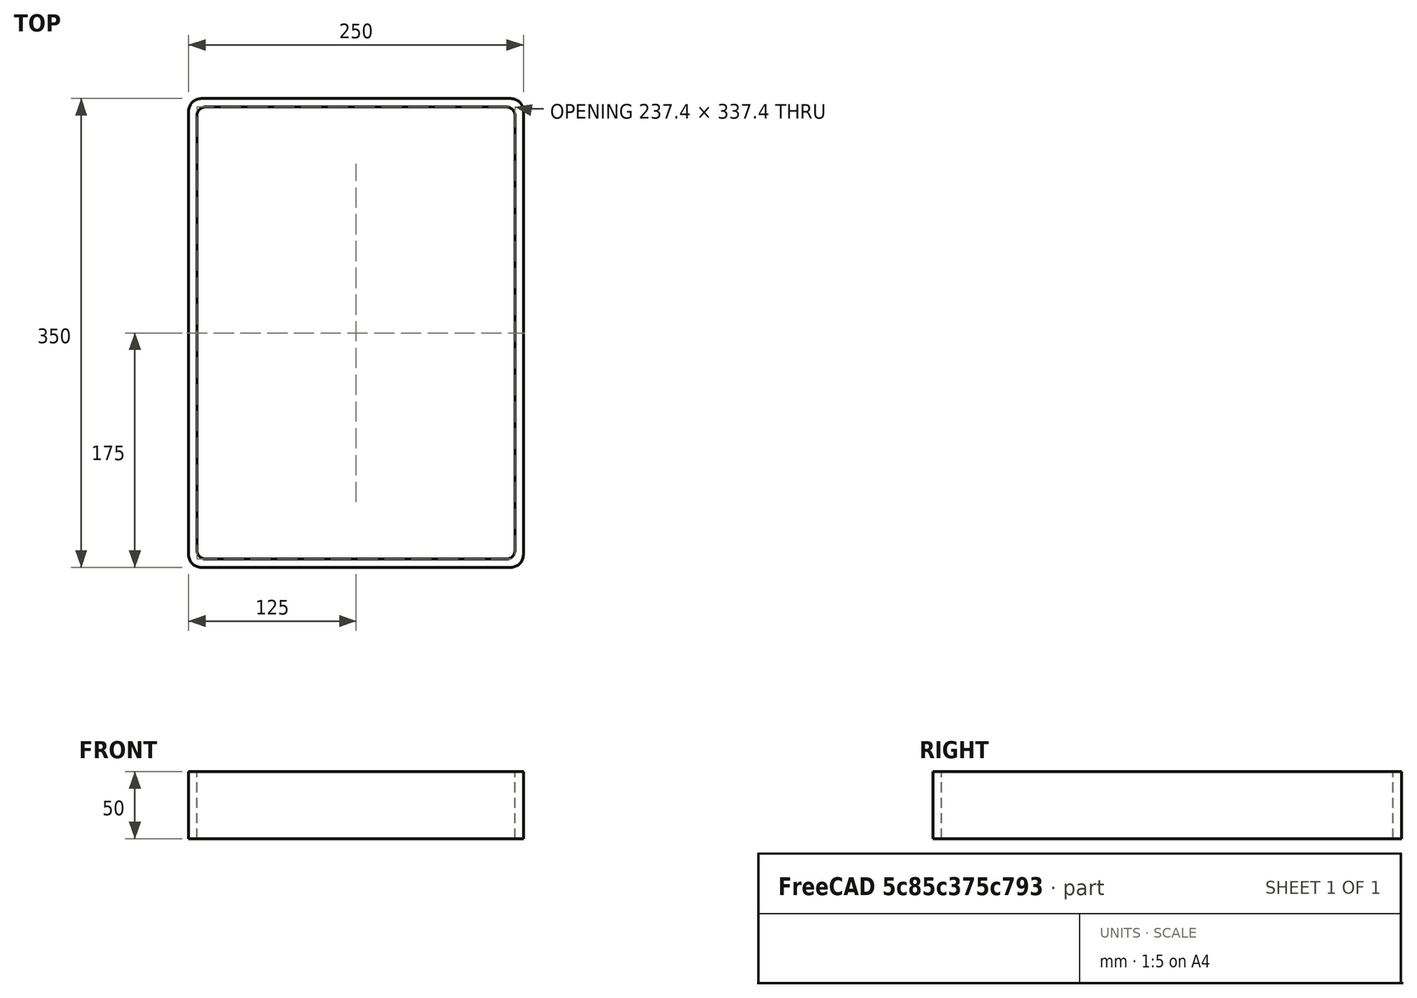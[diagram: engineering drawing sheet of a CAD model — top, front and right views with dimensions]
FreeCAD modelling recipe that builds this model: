
FCSTD DOCUMENT  (FreeCAD 0.15R4671 (Git))
Label: Rectangular hollow section 350x250x6.3 EN10219 S235JRH
License: All rights reserved
LicenseURL: http://en.wikipedia.org/wiki/All_rights_reserved
objects: Sketcher::SketchObject×1, Part::Extrusion×1
note: 2 computed .brp shape members not serialized (recipe doc carries the construction recipe); baked Part::Feature solids carry a one-line shape summary decoded from their .brp

FEATURE [Sketcher::SketchObject] Sketch
  sketch-geometry (16):
    g0: LineSegment StartX=-112.4 StartY=168.7 StartZ=0 EndX=112.4 EndY=168.7 EndZ=0
    g1: LineSegment StartX=118.7 StartY=162.4 StartZ=0 EndX=118.7 EndY=-162.4 EndZ=0
    g2: LineSegment StartX=112.4 StartY=-168.7 StartZ=0 EndX=-112.4 EndY=-168.7 EndZ=0
    g3: LineSegment StartX=-118.7 StartY=-162.4 StartZ=0 EndX=-118.7 EndY=162.4 EndZ=0
    g4: LineSegment StartX=-115.55 StartY=175 StartZ=0 EndX=115.55 EndY=175 EndZ=0
    g5: LineSegment StartX=125 StartY=165.55 StartZ=0 EndX=125 EndY=-165.55 EndZ=0
    g6: LineSegment StartX=115.55 StartY=-175 StartZ=0 EndX=-115.55 EndY=-175 EndZ=0
    g7: LineSegment StartX=-125 StartY=-165.55 StartZ=0 EndX=-125 EndY=165.55 EndZ=0
    g8: ArcOfCircle CenterX=-112.4 CenterY=162.4 CenterZ=0 NormalX=0 NormalY=0 NormalZ=1 Radius=6.3 StartAngle=1.5708 EndAngle=3.14159
    g9: ArcOfCircle CenterX=112.4 CenterY=162.4 CenterZ=0 NormalX=0 NormalY=0 NormalZ=1 Radius=6.3 StartAngle=0 EndAngle=1.5708
    g10: ArcOfCircle CenterX=112.4 CenterY=-162.4 CenterZ=0 NormalX=0 NormalY=0 NormalZ=1 Radius=6.3 StartAngle=4.71239 EndAngle=6.28319
    g11: ArcOfCircle CenterX=-112.4 CenterY=-162.4 CenterZ=0 NormalX=0 NormalY=0 NormalZ=1 Radius=6.3 StartAngle=3.14159 EndAngle=4.71239
    g12: ArcOfCircle CenterX=115.55 CenterY=165.55 CenterZ=0 NormalX=0 NormalY=0 NormalZ=1 Radius=9.45 StartAngle=0 EndAngle=1.5708
    g13: ArcOfCircle CenterX=115.55 CenterY=-165.55 CenterZ=0 NormalX=0 NormalY=0 NormalZ=1 Radius=9.45 StartAngle=4.71239 EndAngle=6.28319
    g14: ArcOfCircle CenterX=-115.55 CenterY=-165.55 CenterZ=0 NormalX=0 NormalY=0 NormalZ=1 Radius=9.45 StartAngle=3.14159 EndAngle=4.71239
    g15: ArcOfCircle CenterX=-115.55 CenterY=165.55 CenterZ=0 NormalX=0 NormalY=0 NormalZ=1 Radius=9.45 StartAngle=1.5708 EndAngle=3.14159
  constraints (36):
    c: Horizontal(g2)
    c: Vertical(g3)
    c: Horizontal(g6)
    c: Vertical(g7)
    c: Tangent(g3,g8) = 1.5708
    c: Tangent(g0,g8) = 1.5708
    c: Tangent(g0,g9) = 1.5708
    c: Tangent(g1,g9) = 1.5708
    c: Tangent(g1,g10) = 1.5708
    c: Tangent(g2,g10) = 1.5708
    c: Tangent(g2,g11) = 1.5708
    c: Tangent(g3,g11) = 1.5708
    c: Tangent(g4,g12) = 1.5708
    c: Tangent(g5,g12) = 1.5708
    c: Tangent(g5,g13) = 1.5708
    c: Tangent(g6,g13) = 1.5708
    c: Tangent(g6,g14) = 1.5708
    c: Tangent(g7,g14) = 1.5708
    c: Tangent(g7,g15) = 1.5708
    c: Tangent(g4,g15) = 1.5708
    c: Equal(g9,g8)
    c: Equal(g9,g11)
    c: Equal(g9,g10)
    c: Equal(g12,g15)
    c: Equal(g12,g14)
    c: Equal(g12,g13)
    c: Symmetric(g4,g6,g-1)
    c: Symmetric(g7,g5,g-2)
    c: DistanceY(g4,g6) = -350
    c: DistanceX(g7,g5) = 250
    c: Symmetric(g3,g1,g-2)
    c: Symmetric(g0,g2,g-1)
    c: DistanceY(g0,g4) = 6.3
    c: DistanceX(g5,g1) = -6.3
    c: Radius(g9) = 6.3
    c: Radius(g12) = 9.45
FEATURE [Part::Extrusion] Extrude  label="Rectangular hollow section 350x250x6.3 EN10219 S235JRH"
  Base = -> Sketch
  Dir = (0,0,50)
  Solid = true
